# Revit family: 418BBF
name_source: partatom
category: Plumbing Fixtures
revit_build: Autodesk Revit MEP 2016 (Build: 20150220_1215(x64)
units: mm (PartAtom-declared; Revit-internal decimal feet)

## family parameters
Cut with Voids When Loaded = No
Host = Face
OmniClass Number = 23.45.05.14.17
OmniClass Title = Showers
Part Type = Normal
Room Calculation Point = No
Round Connector Dimension = Use Diameter
Shared = Yes

## types (1)
- 418BBF
    -0 Electronic Valves, Single Temp. Metering (Specify Type Where Indicated) = No
    -1 Flush-Mounted ADA Showers = Yes
    -5 Flo-Cloz, Single Temp (w/ Lever Handle) = No
    -6 Air-Control, Single Temperature Metering = No
    -8 T/P Temperature-Pressure Balancing Mixing Valve With Patented Ligature Resistant ADA Tri-Lever Handle (ASSE 1016 Compliant) = Yes
    -BS Built-in Liquid Soap System (Dispenser Not ADA Compliant) = No
    -CH Curtain with Headrail - 36" Opening = No
    -CI Cycle Interrupt for Time-Trol Valves = No
    -CSH Conical Showerhead (Ligature Resistant) = No
    -D Soap Dish = No
    -EG Enviro-Glaze (Specify Color) = No
    -EH Extended Head 17.5 Degree Discharge = No
    -EVS1 Electronic Valve System - Single Temp = No
    -EVSP1 Electronic Valve Sys. w/ Piezo Pushbutton = No
    -F Flow Control   2.0GPM (No Longer Available in California) = No
    -FG - 14 Gage Panel = No
    -FSP Phenolic Folding Seat in Lieu of Padded Seat = No
    -FSS Stainless Steel Folding Seat in Lieu of Padded Seat = No
    -G Individual Stops (Flo-Cloz Only) = No
    -H Hand Voplume Control = No
    -HL Hi-Lo FX Bracket = No
    -K Allen Key Volume Control = No
    -LFS Less Padded Folding Seat = No
    -LGB Less Grab Bar = No
    -LRD Less Recessed Soap Dish = No
    -LVR Lever Handle (-5 & -8 Valve Only) = No
    -MS Modular Privacy Compartments (See Diana Privacy Tab) = No
    -MSH Multi-Stream Showerhead = No
    -MTP1 Electronic Valve Sys. w/ Single Temp = No
    -MTPP1 Electronic Valve Sys. w/ Single Temp Piezo Pushbutton = No
    -MVC1 Time-Trol - Single Temp = No
    -P Penal Showerhead = No
    -PBH Hemispherical Pushbutton = No
    -PPZ1 Programmable Piezo Pushbutton (Single Temperature Only) = No
    -PSO  Positive Shut-Off for Quick Disconnect = No
    -RP Reinforced Panel for Folding Seat with Curtain = No
    -SB 24" Slide Bar (Panel Mounted) = No
    -TF Transformer, 120VAC to 24VAC (-MVC option only) = No
    -W Wall = No
    -WS Without Showerhead = No
    -Y Universal Ball Joint = No
    -YY Lockable Universal Ball Joint = No
    -Z Up-Down Ball Joint = No
    -ZZ Lockable Up-Down Ball Joint = No
    4 - Apex = Yes
    Assembly Code = D2010710
    CW Connection = Yes
    CWFU = 2
    Default Elevation = 55"
    Description = Acorn Shower-Ware® 410BADA Series Apex Type 1, Flush-Mounted Showers - ADA Compliant
    HW Connection = Yes
    HWFU = 3
    Manufacturer = Acorn Engineering Company
    Material = Stainless Steel-Acorn-Type 304-Satin
    Model = 418BADA
    Revised Date = 09/21/2015
    URL = http://www.acorneng.com
    Vent Connection = No
    WFU = 4
    Waste Connection = No

## geometry (parser evidence)
native form markers: Sweep x12
no freeform markers — native parametric forms only
